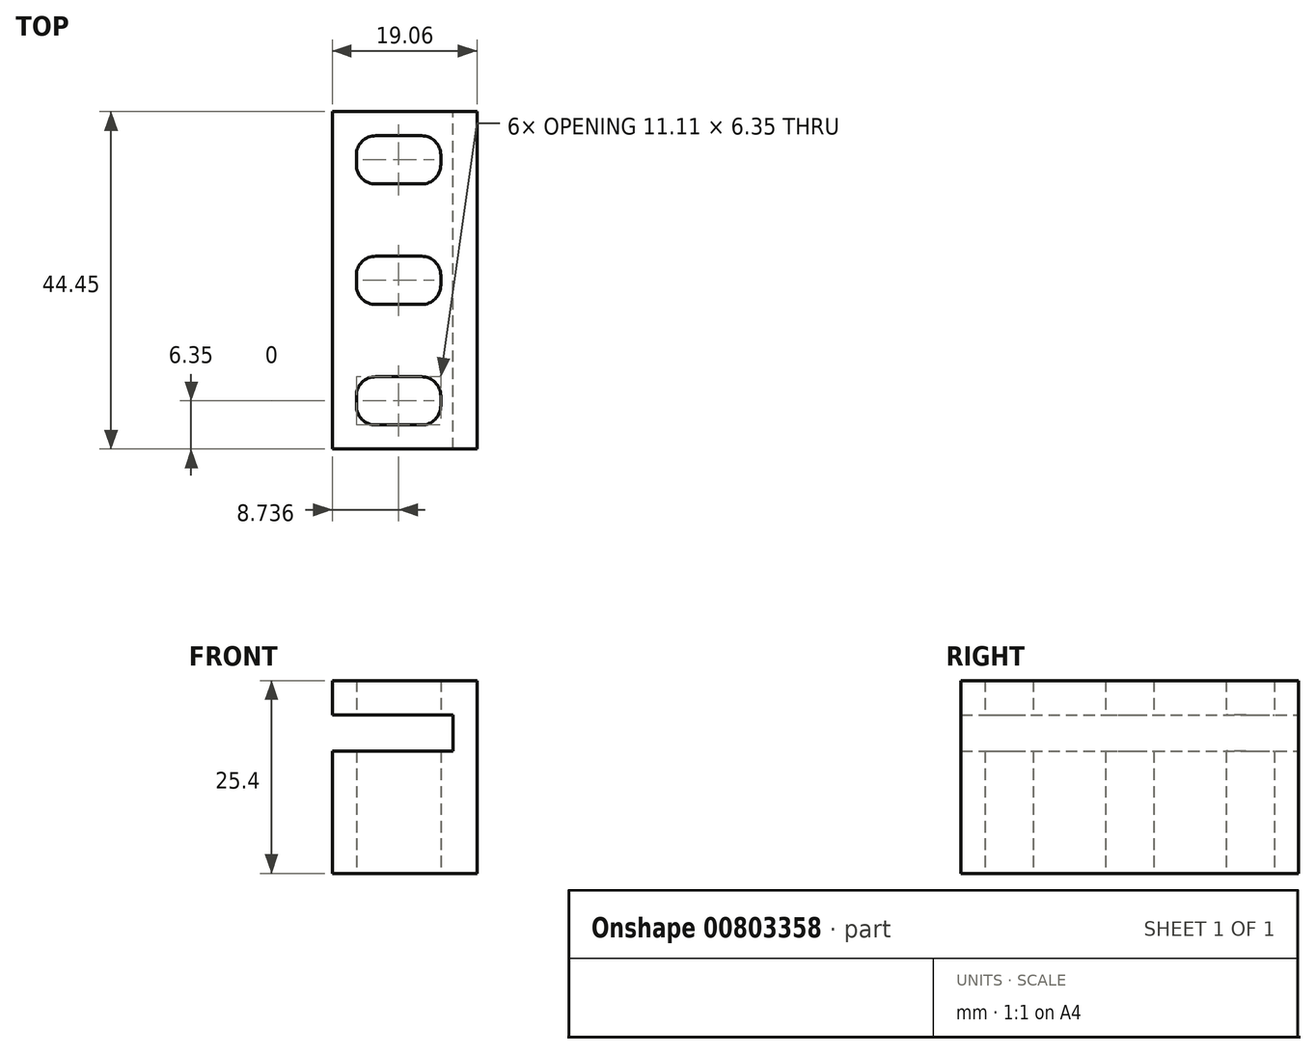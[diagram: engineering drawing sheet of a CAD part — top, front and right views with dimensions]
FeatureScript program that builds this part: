
annotation { "Feature Type Name" : "Feature", "Feature Type Description" : "" }
export const myFeature = defineFeature(function(context is Context, id is Id, definition is map)
    precondition{}
    {
        {
            var Q0;
            Q0=qCreatedBy(makeId("Top.planeOp"),FACE);
            var sketch = newSketch(context, id + "F0", { "sketchPlane" : qUnion([Q0])});
            skLineSegment(sketch, "E0.bottom", {"start": v(-9.53, 0) * mm, "end": v(9.53, 0) * mm});
            skLineSegment(sketch, "E0.top", {"start": v(-9.53, -44.45) * mm, "end": v(9.53, -44.45) * mm});
            skLineSegment(sketch, "E0.left", {"start": v(-9.53, 0) * mm, "end": v(-9.53, -44.45) * mm});
            skLineSegment(sketch, "E0.right", {"start": v(9.53, 0) * mm, "end": v(9.53, -44.45) * mm});
            skLineSegment(sketch, "E1.bottom", {"start": v(-3.8, -3.18) * mm, "end": v(2.22, -3.17) * mm});
            skLineSegment(sketch, "E1.top", {"start": v(-3.8, -9.53) * mm, "end": v(2.22, -9.53) * mm});
            skLineSegment(sketch, "E1.left", {"start": v(-6.35, -5.72) * mm, "end": v(-6.35, -6.99) * mm});
            skLineSegment(sketch, "E1.right", {"start": v(4.76, -5.71) * mm, "end": v(4.76, -6.98) * mm});
            skPoint(sketch, "E2.visualSharp", {"position": v(-6.35, -3.18) * mm});
            skArc(sketch, "E2.filletArc", {"start": v(-3.8, -3.18) * mm, "mid": v(-5.6, -3.92) * mm, "end": v(-6.35, -5.72) * mm});
            skPoint(sketch, "E3.visualSharp", {"position": v(-6.35, -9.53) * mm});
            skArc(sketch, "E3.filletArc", {"start": v(-6.35, -6.99) * mm, "mid": v(-5.6, -8.78) * mm, "end": v(-3.8, -9.53) * mm});
            skPoint(sketch, "E4.visualSharp", {"position": v(4.76, -3.17) * mm});
            skArc(sketch, "E4.filletArc", {"start": v(4.76, -5.71) * mm, "mid": v(4.02, -3.92) * mm, "end": v(2.22, -3.17) * mm});
            skPoint(sketch, "E5.visualSharp", {"position": v(4.76, -9.52) * mm});
            skArc(sketch, "E5.filletArc", {"start": v(2.22, -9.52) * mm, "mid": v(4.02, -8.78) * mm, "end": v(4.76, -6.98) * mm});
            skLineSegment(sketch, "E6.bottom", {"start": v(-3.8, -34.93) * mm, "end": v(2.22, -34.93) * mm});
            skLineSegment(sketch, "E6.top", {"start": v(-3.8, -41.28) * mm, "end": v(2.22, -41.28) * mm});
            skLineSegment(sketch, "E6.left", {"start": v(-6.35, -37.47) * mm, "end": v(-6.35, -38.74) * mm});
            skLineSegment(sketch, "E6.right", {"start": v(4.76, -37.47) * mm, "end": v(4.76, -38.74) * mm});
            skPoint(sketch, "E7.visualSharp", {"position": v(-6.35, -34.93) * mm});
            skArc(sketch, "E7.filletArc", {"start": v(-3.8, -34.93) * mm, "mid": v(-5.6, -35.67) * mm, "end": v(-6.35, -37.47) * mm});
            skPoint(sketch, "E8.visualSharp", {"position": v(-6.35, -41.28) * mm});
            skArc(sketch, "E8.filletArc", {"start": v(-6.35, -38.74) * mm, "mid": v(-5.6, -40.53) * mm, "end": v(-3.8, -41.28) * mm});
            skPoint(sketch, "E9.visualSharp", {"position": v(4.76, -41.28) * mm});
            skArc(sketch, "E9.filletArc", {"start": v(2.22, -41.28) * mm, "mid": v(4.02, -40.53) * mm, "end": v(4.76, -38.74) * mm});
            skPoint(sketch, "E10.visualSharp", {"position": v(4.76, -34.93) * mm});
            skArc(sketch, "E10.filletArc", {"start": v(4.76, -37.47) * mm, "mid": v(4.02, -35.67) * mm, "end": v(2.22, -34.93) * mm});
            skLineSegment(sketch, "E11.bottom", {"start": v(-3.8, -19.05) * mm, "end": v(2.22, -19.05) * mm});
            skLineSegment(sketch, "E11.top", {"start": v(-3.8, -25.4) * mm, "end": v(2.22, -25.4) * mm});
            skLineSegment(sketch, "E11.left", {"start": v(-6.35, -21.59) * mm, "end": v(-6.35, -22.86) * mm});
            skLineSegment(sketch, "E11.right", {"start": v(4.76, -21.59) * mm, "end": v(4.76, -22.86) * mm});
            skPoint(sketch, "E12.visualSharp", {"position": v(-6.35, -19.05) * mm});
            skArc(sketch, "E12.filletArc", {"start": v(-3.8, -19.05) * mm, "mid": v(-5.6, -19.8) * mm, "end": v(-6.35, -21.59) * mm});
            skPoint(sketch, "E13.visualSharp", {"position": v(-6.35, -25.4) * mm});
            skArc(sketch, "E13.filletArc", {"start": v(-6.35, -22.86) * mm, "mid": v(-5.6, -24.66) * mm, "end": v(-3.8, -25.4) * mm});
            skPoint(sketch, "E14.visualSharp", {"position": v(4.76, -25.4) * mm});
            skArc(sketch, "E14.filletArc", {"start": v(2.22, -25.4) * mm, "mid": v(4.02, -24.66) * mm, "end": v(4.76, -22.86) * mm});
            skPoint(sketch, "E15.visualSharp", {"position": v(4.76, -19.05) * mm});
            skArc(sketch, "E15.filletArc", {"start": v(4.76, -21.59) * mm, "mid": v(4.02, -19.8) * mm, "end": v(2.22, -19.05) * mm});
            skSolve(sketch);
        }
        {
            var Q0;
            Q0=makeQuery(id+"F0.imprint","IMPRINT",FACE,{"disambiguationData":[TD([[makeQuery(id+"F0.imprint","IMPRINT",EDGE,{"derivedFrom":sQuery(id+"F0.wireOp",EDGE,"E0.bottom")}),-1.0]])]});
            extrude(context, id + "F1", {"entities" : qUnion([Q0]), "depth" : 25.4 * mm, "offsetDistance" : 25.4 * mm});
        }
        {
            var Q0;
            Q0=makeQuery(id+"F1.opExtrude","SWEPT_FACE",FACE,{"disambiguationData":[OSD([sQuery(id+"F0.wireOp",EDGE,"E0.bottom")])]});
            var sketch = newSketch(context, id + "F2", { "sketchPlane" : qUnion([Q0])});
            skLineSegment(sketch, "E16.bottom", {"start": v(-6.35, 20.86) * mm, "end": v(19.05, 20.86) * mm});
            skLineSegment(sketch, "E16.top", {"start": v(-6.35, 16.1) * mm, "end": v(19.05, 16.1) * mm});
            skLineSegment(sketch, "E16.left", {"start": v(-6.35, 20.86) * mm, "end": v(-6.35, 16.1) * mm});
            skLineSegment(sketch, "E16.right", {"start": v(19.05, 20.86) * mm, "end": v(19.05, 16.1) * mm});
            skSolve(sketch);
        }
        {
            var Q0;
            {var subQ0=sQuery(id+"F2.wireOp",EDGE,"E16.left");Q0=makeQuery(id+"F2.imprint","IMPRINT",FACE,{"disambiguationData":[TD([[makeQuery(id+"F2.imprint","IMPRINT",EDGE,{"derivedFrom":subQ0}),1.0]])]});}
            var Q1;
            {var subQ0=sQuery(id+"F2.wireOp",EDGE,"E16.right");Q1=makeQuery(id+"F2.imprint","IMPRINT",FACE,{"disambiguationData":[TD([[makeQuery(id+"F2.imprint","IMPRINT",EDGE,{"derivedFrom":subQ0}),-1.0]])]});}
            extrude(context, id + "F3", {"entities" : qUnion([Q0, Q1]), "operationType" : NewBodyOperationType.REMOVE, "oppositeDirection" : true, "depth" : 45.97 * mm, "offsetDistance" : 25.4 * mm});
        }
    });
